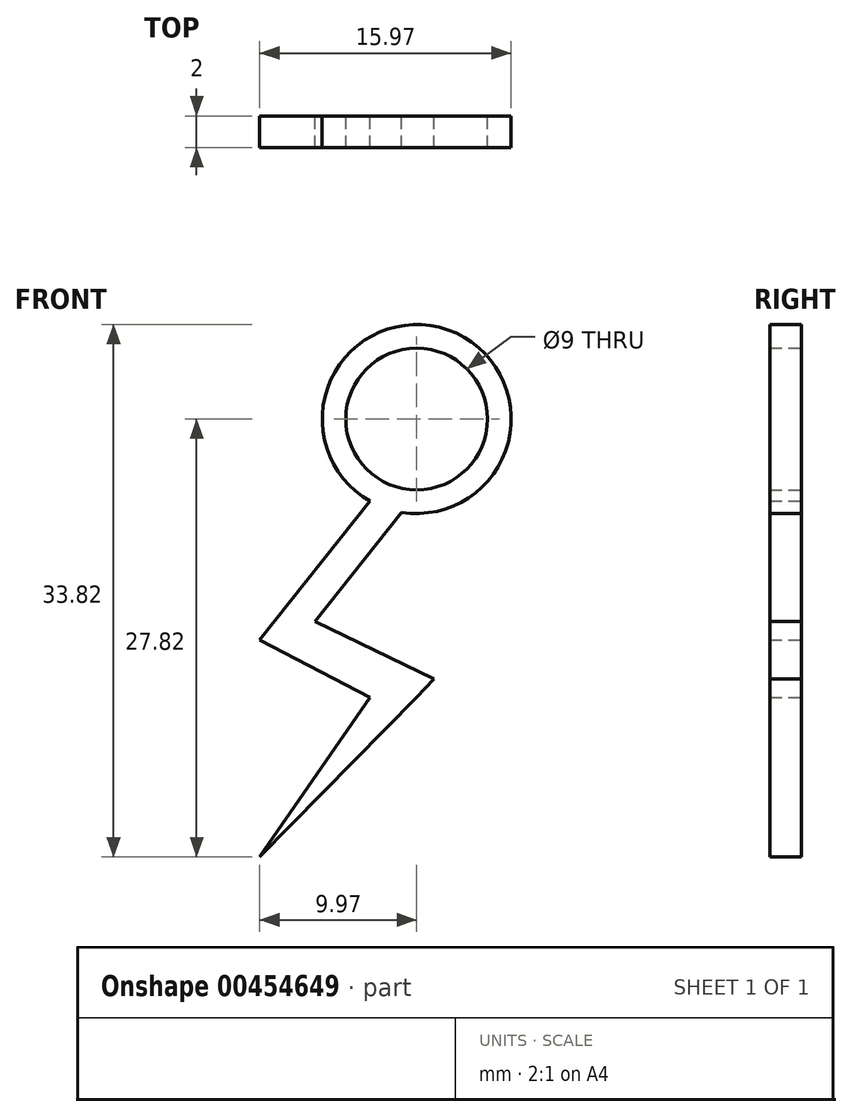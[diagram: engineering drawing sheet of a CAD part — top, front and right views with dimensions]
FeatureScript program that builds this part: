
annotation { "Feature Type Name" : "Feature", "Feature Type Description" : "" }
export const myFeature = defineFeature(function(context is Context, id is Id, definition is map)
    precondition{}
    {
        {
            var Q0;
            Q0=qCreatedBy(makeId("Front.planeOp"),FACE);
            var sketch = newSketch(context, id + "F0", { "sketchPlane" : qUnion([Q0])});
            skCircle(sketch, "E0", {"center": v(0, 0) * mm, "radius": 4.5 * mm});
            skArc(sketch, "E1", {"start": v(-0.95, -5.92) * mm, "mid": v(1.98, 5.66) * mm, "end": v(-2.95, -5.22) * mm});
            skPoint(sketch, "E2.trimOffspring.end.orphan", {"position": v(0, -4.29) * mm});
            skLineSegment(sketch, "E3", {"start": v(-2.95, -5.22) * mm, "end": v(-9.97, -14.05) * mm});
            skLineSegment(sketch, "E4", {"start": v(-9.97, -14.05) * mm, "end": v(-2.95, -17.67) * mm});
            skLineSegment(sketch, "E5", {"start": v(-2.95, -17.67) * mm, "end": v(-9.97, -27.82) * mm});
            skLineSegment(sketch, "E6", {"start": v(-9.97, -27.82) * mm, "end": v(0, -17.67) * mm});
            skLineSegment(sketch, "E7", {"start": v(-0.95, -5.92) * mm, "end": v(-6.46, -12.85) * mm});
            skPoint(sketch, "E7.endSnap0", {"position": v(-6.46, -9.63) * mm});
            skLineSegment(sketch, "E8", {"start": v(-6.46, -12.85) * mm, "end": v(1.1, -16.52) * mm});
            skLineSegment(sketch, "E9", {"start": v(0, -17.67) * mm, "end": v(1.1, -16.52) * mm});
            skSolve(sketch);
        }
        {
            var Q0;
            Q0 = qSketchRegion(id + "F0", true);
            extrude(context, id + "F1", {"entities" : qUnion([Q0]), "depth" : 2 * mm, "offsetDistance" : 25 * mm});
        }
    });
